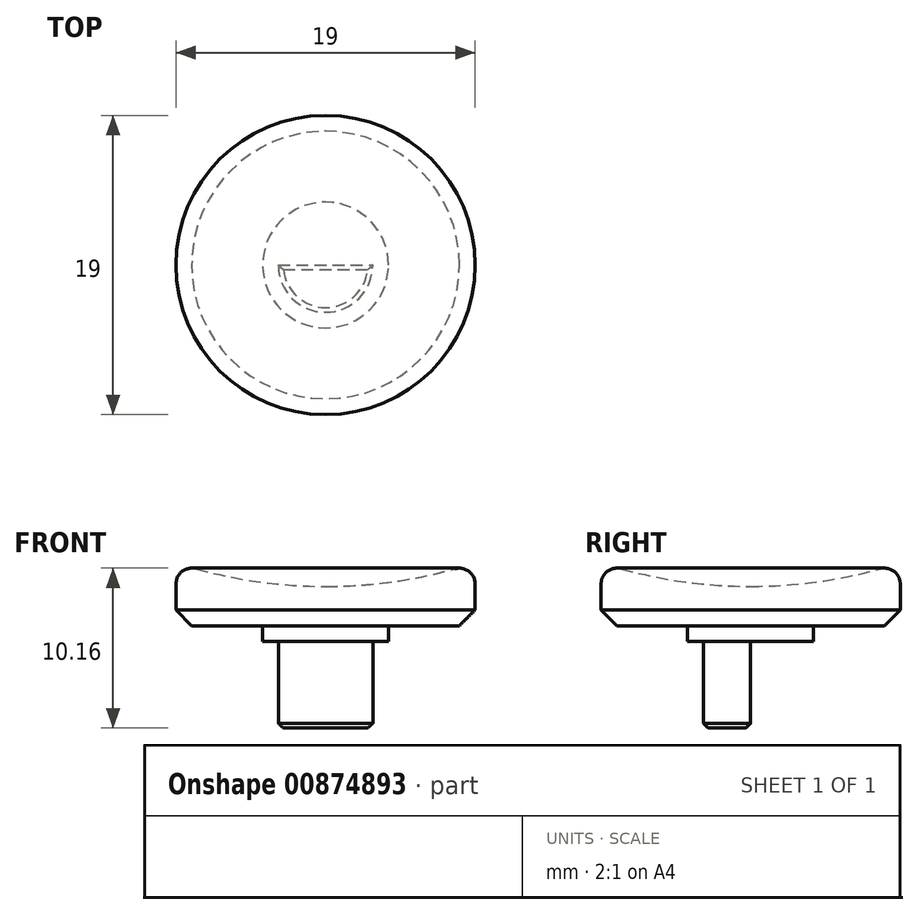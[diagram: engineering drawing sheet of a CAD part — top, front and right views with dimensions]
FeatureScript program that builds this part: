
annotation { "Feature Type Name" : "Feature", "Feature Type Description" : "" }
export const myFeature = defineFeature(function(context is Context, id is Id, definition is map)
    precondition{}
    {
        {
            var Q0;
            Q0=qCreatedBy(makeId("Front.planeOp"),FACE);
            var sketch = newSketch(context, id + "F0", { "sketchPlane" : qUnion([Q0])});
            skArc(sketch, "E0", {"start": v(0, 2.5) * mm, "mid": v(4.8, 2.88) * mm, "end": v(9.5, 4) * mm});
            skLineSegment(sketch, "E1", {"start": v(0, 2.5) * mm, "end": v(0, 0) * mm});
            skLineSegment(sketch, "E2", {"start": v(0, 0) * mm, "end": v(9.5, 0) * mm});
            skLineSegment(sketch, "E3", {"start": v(9.5, 0) * mm, "end": v(9.5, 4) * mm});
            skLineSegment(sketch, "E4", {"start": v(0, 2.5) * mm, "end": v(-3.82, 2.5) * mm, "construction": true});
            skLineSegment(sketch, "E5", {"start": v(0, 0) * mm, "end": v(0, -1) * mm});
            skLineSegment(sketch, "E6", {"start": v(0, -1) * mm, "end": v(4, -1) * mm});
            skLineSegment(sketch, "E7", {"start": v(4, -1) * mm, "end": v(4, 0) * mm});
            skSolve(sketch);
        }
        {
            var Q0;
            Q0=makeQuery(id+"F0.imprint","IMPRINT",FACE,{"disambiguationData":[TD([[makeQuery(id+"F0.imprint","IMPRINT",EDGE,{"derivedFrom":sQuery(id+"F0.wireOp",EDGE,"E0")}),-1.0]])]});
            var Q1;
            {var subQ0=sQuery(id+"F0.wireOp",EDGE,"E5");Q1=makeQuery(id+"F0.imprint","IMPRINT",FACE,{"disambiguationData":[TD([[makeQuery(id+"F0.imprint","IMPRINT",EDGE,{"derivedFrom":subQ0}),1.0]])]});}
            var Q2;
            Q2=sQuery(id+"F0.wireOp",EDGE,"E1");
            revolve(context, id + "F1", {"surfaceOperationType" : NewSurfaceOperationType.NEW, "entities" : qUnion([Q0, Q1]), "axis" : qUnion([Q2]), "revolveType" : RevolveType.FULL});
        }
        {
            var Q0;
            Q0=makeQuery(id+"F1.opRevolve","SWEPT_EDGE",EDGE,{"disambiguationData":[OSD([sQuery(id+"F0.wireOp",EDGE,"E2"),sQuery(id+"F0.wireOp",EDGE,"E3")])]});
            chamfer(context, id + "F2", {"entities" : qUnion([Q0]), "width" : 1 * mm, "tangentPropagation" : true});
        }
        {
            var Q0;
            Q0=makeQuery(id+"F1.opRevolve","SWEPT_EDGE",EDGE,{"disambiguationData":[OSD([sQuery(id+"F0.wireOp",EDGE,"E0"),sQuery(id+"F0.wireOp",EDGE,"E3")])]});
            fillet(context, id + "F3", {"entities" : qUnion([Q0]), "radius" : 1 * mm, "tangentPropagation" : true, "allowEdgeOverflow" : false});
        }
        {
            var Q0;
            Q0=makeQuery(id+"F1.opRevolve","SWEPT_FACE",FACE,{"disambiguationData":[OSD([sQuery(id+"F0.wireOp",EDGE,"E6")])]});
            var sketch = newSketch(context, id + "F4", { "sketchPlane" : qUnion([Q0])});
            skCircle(sketch, "E8", {"center": v(0, 0) * mm, "radius": 3 * mm});
            skLineSegment(sketch, "E9", {"start": v(-3, 0) * mm, "end": v(3, 0) * mm});
            skSolve(sketch);
        }
        {
            var Q0;
            {var subQ0=sQuery(id+"F4.wireOp",EDGE,"E9");Q0=makeQuery(id+"F4.imprint","IMPRINT",FACE,{"disambiguationData":[TD([[makeQuery(id+"F4.imprint","IMPRINT",EDGE,{"derivedFrom":subQ0}),1.0]])]});}
            extrude(context, id + "F5", {"entities" : qUnion([Q0]), "operationType" : NewBodyOperationType.ADD, "depth" : 5.5 * mm, "offsetDistance" : 25 * mm});
        }
        {
            var Q0;
            {var subQ0=sQuery(id+"F4.wireOp",EDGE,"E9");var subQ1=sQuery(id+"F4.wireOp",EDGE,"E8");var subQ2=makeQuery(id+"F4.imprint","INTERSECT",VERTEX,{"disambiguationData":[OD(1.0)],"derivedFrom":[subQ1,subQ0]});var subQ3=sQuery(id+"F4.wireOp",EDGE,"EuXthmaV-2YND-Fm3C-13Ho-nnoiFGs2Bl0C");var subQ4=makeQuery(id+"F4.imprint","INTERSECT",VERTEX,{"disambiguationData":[OD(0.0)],"derivedFrom":[subQ3,subQ0]});var subQ5=sQuery(id+"F4.wireOp",EDGE,"RgohzL3Y-MxSy-Aeoz-WfzF-u7yks00zWtu8");var subQ6=makeQuery(id+"F4.imprint","INTERSECT",VERTEX,{"disambiguationData":[OD(1.0)],"derivedFrom":[subQ1,subQ5]});Q0=makeQuery(id+"F5.opExtrude","CAP_FACE",FACE,{"disambiguationData":[OSD([subQ3,subQ1,subQ5,subQ0]),TDD([makeQuery(id+"F4.imprint","IMPRINT",EDGE,{"disambiguationData":[TD([[subQ4,1.0]])],"derivedFrom":subQ3}),makeQuery(id+"F4.imprint","IMPRINT",EDGE,{"disambiguationData":[TD([[subQ6,-1.0]])],"derivedFrom":subQ1}),makeQuery(id+"F4.imprint","IMPRINT",EDGE,{"disambiguationData":[TD([[subQ6,1.0]])],"derivedFrom":subQ5}),makeQuery(id+"F4.imprint","IMPRINT",EDGE,{"disambiguationData":[TD([[subQ2,1.0]])],"derivedFrom":subQ0})])],"isStart":false});}
            var Q1;
            {var subQ0=sQuery(id+"F4.wireOp",EDGE,"E9");var subQ1=sQuery(id+"F4.wireOp",EDGE,"E8");var subQ2=makeQuery(id+"F4.imprint","INTERSECT",VERTEX,{"disambiguationData":[OD(0.0)],"derivedFrom":[subQ1,subQ0]});var subQ3=sQuery(id+"F4.wireOp",EDGE,"EuXthmaV-2YND-Fm3C-13Ho-nnoiFGs2Bl0C");var subQ5=sQuery(id+"F4.wireOp",EDGE,"RgohzL3Y-MxSy-Aeoz-WfzF-u7yks00zWtu8");var subQ6=makeQuery(id+"F4.imprint","INTERSECT",VERTEX,{"disambiguationData":[OD(0.0)],"derivedFrom":[subQ1,subQ5]});var subQ7=makeQuery(id+"F4.imprint","INTERSECT",VERTEX,{"disambiguationData":[OD(0.0)],"derivedFrom":[subQ3,subQ5]});Q1=makeQuery(id+"F5.opExtrude","CAP_FACE",FACE,{"disambiguationData":[OSD([subQ3,subQ1,subQ5,subQ0]),TDD([makeQuery(id+"F4.imprint","IMPRINT",EDGE,{"disambiguationData":[TD([[subQ7,-1.0]])],"derivedFrom":subQ3}),makeQuery(id+"F4.imprint","IMPRINT",EDGE,{"disambiguationData":[TD([[subQ6,-1.0]])],"derivedFrom":subQ1}),makeQuery(id+"F4.imprint","IMPRINT",EDGE,{"disambiguationData":[TD([[subQ6,-1.0]])],"derivedFrom":subQ5}),makeQuery(id+"F4.imprint","IMPRINT",EDGE,{"disambiguationData":[TD([[subQ2,-1.0]])],"derivedFrom":subQ0})])],"isStart":false});}
            chamfer(context, id + "F6", {"entities" : qUnion([Q0, Q1]), "width" : 0.3 * mm, "tangentPropagation" : true});
        }
    });
